# Revit family: 71914
name_source: partatom
category: Lighting Fixtures
revit_build: Autodesk Revit 2018 (Build: 20190510_1515(x64)
units: mm (PartAtom-declared; Revit-internal decimal feet)

## family parameters
Always vertical = No
Cut with Voids When Loaded = Yes
Light Source = No
OmniClass Number = 23.80.70.00
OmniClass Title = Lighting
Part Type = Normal
Room Calculation Point = No
Round Connector Dimension = Use Diameter
Shared = No
Work Plane-Based = Yes

## types (3) — shared parameters
Default Elevation = 1219 mm
FARO_Category = Outdoor
FARO_Description EN = KASP Wall lamp accessory
FARO_Description ES = KASP Accesorio aplique
FARO_Last Actualization Date = 29/04/2021
FARO_Material_01 = FARO_Black Matt
FARO_Material_02 = FARO_Black ceramics
FARO_Material_03 = FARO_White_translucide
FARO_Material_04 = FARO_Black Matt
FARO_Model Line = KASP
FARO_Ref = 71914
FARO_Subcategory = Portable
Hand.aux = 74 mm
Manufacturer = FARO Barcelona
URL = https://www.faro.es

## per-type parameters (varying)
| type | FARO_EAN | FARO_Ref_Accessory | FARO_URL Model | Heigth | KASP lamp | Pendant height |
| 71914 KASP Wall lamp accessory | 8421776240285 | for 71912, 71913 | https://faro.es | 502 mm | No | 575 mm |
| 71914 KASP Wall lamp accessory + 71912 |  | 71912 |  | 302 mm | Yes | 375 mm |
| 71914 KASP Wall lamp accessory + 71913 |  | 71913 |  | 502 mm | Yes | 575 mm |

## geometry (parser evidence)
native form markers: Sweep x10
no freeform markers — native parametric forms only
